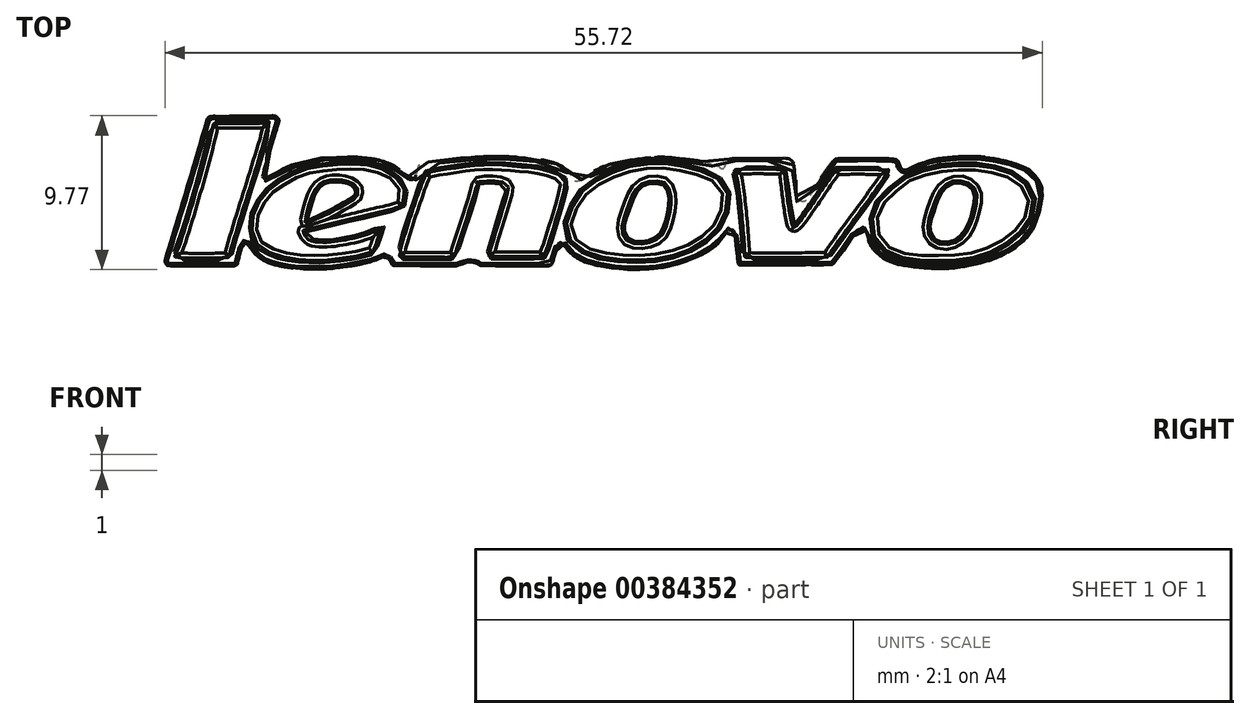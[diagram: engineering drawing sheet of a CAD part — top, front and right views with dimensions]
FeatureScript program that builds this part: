
annotation { "Feature Type Name" : "Feature", "Feature Type Description" : "" }
export const myFeature = defineFeature(function(context is Context, id is Id, definition is map)
    precondition{}
    {
        {
            var Q0;
            Q0=qCreatedBy(makeId("Top.planeOp"),FACE);
            var sketch = newSketch(context, id + "F0", { "sketchPlane" : qUnion([Q0])});
            skFitSpline(sketch, "E0", {"points": [v(-23.1, 6.55) * mm, v(-23.35, 5.6) * mm, v(-23.4, 5.47) * mm, v(-23.53, 5.4) * mm, v(-23.82, 5.4) * mm, v(-27.77, 5.41) * mm, v(-27.88, 5.47) * mm, v(-27.96, 5.64) * mm, v(-27.93, 5.83) * mm, v(-25.31, 14.6) * mm, v(-25.25, 14.76) * mm, v(-25.1, 14.86) * mm, v(-24.75, 14.9) * mm, v(-21.3, 14.92) * mm, v(-20.98, 14.9) * mm, v(-20.82, 14.8) * mm, v(-20.74, 14.67) * mm, v(-20.77, 14.44) * mm, v(-21.75, 11.14) * mm, v(-21.74, 10.99) * mm, v(-21.66, 10.94) * mm, v(-21.44, 10.94) * mm, v(-20.73, 11.4) * mm, v(-19.83, 11.81) * mm, v(-19.1, 12.04) * mm, v(-18.16, 12.23) * mm, v(-17.27, 12.3) * mm, v(-16.19, 12.3) * mm, v(-15.44, 12.26) * mm, v(-14.56, 12.15) * mm, v(-13.8, 11.92) * mm, v(-13.19, 11.6) * mm, v(-12.82, 11.28) * mm, v(-12.63, 11.03) * mm, v(-12.42, 10.87) * mm, v(-12.17, 10.91) * mm, v(-12.08, 11.06) * mm, v(-11.93, 11.4) * mm, v(-11.82, 11.79) * mm, v(-11.59, 11.9) * mm, v(-10.16, 12.15) * mm, v(-8.7, 12.26) * mm, v(-7.2, 12.34) * mm, v(-5.86, 12.3) * mm, v(-4.6, 12.19) * mm, v(-3.59, 12.03) * mm, v(-2.83, 11.74) * mm, v(-2.27, 11.31) * mm, v(-2.1, 10.99) * mm, v(-1.96, 10.8) * mm, v(-1.78, 10.78) * mm, v(-1.62, 10.82) * mm, v(-1.3, 10.99) * mm, v(-0.5, 11.52) * mm, v(0.8, 11.97) * mm, v(2.15, 12.17) * mm, v(3.5, 12.3) * mm, v(4.82, 12.19) * mm, v(6.3, 12) * mm, v(7.15, 11.73) * mm, v(7.45, 11.57) * mm, v(7.63, 11.76) * mm, v(7.8, 12.09) * mm, v(7.93, 12.17) * mm, v(8.77, 12.22) * mm, v(10.88, 12.2) * mm, v(11.6, 12.2) * mm, v(11.86, 12.06) * mm, v(12, 11.74) * mm, v(12.06, 11.2) * mm, v(12.11, 10.45) * mm, v(12.18, 9.67) * mm, v(12.45, 9.5) * mm, v(12.76, 9.58) * mm, v(13.74, 11.05) * mm, v(14.3, 11.83) * mm, v(14.57, 12.15) * mm, v(14.75, 12.19) * mm, v(18.37, 12.16) * mm, v(18.52, 12.09) * mm, v(18.62, 11.98) * mm, v(18.7, 11.73) * mm, v(18.9, 11.5) * mm, v(19.19, 11.5) * mm, v(19.75, 11.77) * mm, v(20.26, 11.95) * mm], "startDerivative": vector(-22.6, -79.97) * mm, "endDerivative": vector(46.12, 13.89) * mm});
            skFitSpline(sketch, "E1", {"points": [v(20.26, 11.95) * mm, v(20.8, 12.12) * mm, v(21.55, 12.24) * mm, v(22.57, 12.33) * mm], "startDerivative": vector(1.82, 0.65) * mm, "endDerivative": vector(2.75, 0.2) * mm});
            skFitSpline(sketch, "E2", {"points": [v(22.57, 12.33) * mm, v(23.76, 12.33) * mm, v(25.15, 12.11) * mm, v(26.09, 11.85) * mm, v(26.85, 11.51) * mm, v(27.47, 10.9) * mm, v(27.74, 10.24) * mm, v(27.6, 8.92) * mm, v(27.13, 7.7) * mm, v(26.29, 6.76) * mm, v(24.84, 5.91) * mm, v(23.43, 5.48) * mm, v(21.77, 5.23) * mm, v(20.26, 5.27) * mm, v(18.82, 5.44) * mm, v(17.78, 5.8) * mm, v(16.93, 6.57) * mm, v(16.67, 7.18) * mm, v(16.59, 7.56) * mm, v(16.5, 7.68) * mm, v(16.1, 7.7) * mm, v(15.95, 7.62) * mm, v(15.49, 6.9) * mm, v(14.9, 6.07) * mm, v(14.45, 5.5) * mm, v(14.3, 5.47) * mm, v(8.6, 5.46) * mm, v(8.44, 5.56) * mm, v(8.19, 7.5) * mm, v(8.08, 7.67) * mm, v(7.95, 7.68) * mm, v(7.77, 7.6) * mm, v(7.35, 7.02) * mm, v(6.44, 6.28) * mm, v(5.38, 5.8) * mm, v(3.76, 5.31) * mm, v(2.27, 5.17) * mm, v(1.03, 5.2) * mm, v(-0.32, 5.38) * mm, v(-1.48, 5.73) * mm, v(-2.23, 6.23) * mm, v(-2.57, 6.64) * mm, v(-2.76, 6.84) * mm, v(-2.92, 6.84) * mm, v(-3.02, 6.69) * mm, v(-3.35, 5.64) * mm, v(-3.45, 5.46) * mm, v(-3.6, 5.38) * mm, v(-3.92, 5.37) * mm, v(-7.82, 5.4) * mm, v(-7.93, 5.42) * mm, v(-8.27, 5.58) * mm, v(-8.78, 5.6) * mm, v(-9.34, 5.43) * mm, v(-9.5, 5.4) * mm, v(-13.36, 5.4) * mm, v(-13.49, 5.42) * mm, v(-13.57, 5.56) * mm, v(-13.8, 5.9) * mm, v(-13.95, 6) * mm, v(-14.04, 6) * mm, v(-14.4, 5.82) * mm, v(-15.04, 5.62) * mm, v(-16.03, 5.4) * mm, v(-17.17, 5.25) * mm, v(-18.19, 5.19) * mm, v(-19.33, 5.22) * mm, v(-20.28, 5.31) * mm, v(-21.1, 5.49) * mm, v(-21.75, 5.77) * mm, v(-22.3, 6.22) * mm, v(-22.56, 6.6) * mm, v(-22.67, 6.77) * mm, v(-22.77, 6.86) * mm, v(-22.92, 6.87) * mm, v(-23.03, 6.77) * mm, v(-23.1, 6.55) * mm], "startDerivative": vector(67.8, 2.63) * mm, "endDerivative": vector(-13.05, -26.65) * mm});
            skFitSpline(sketch, "E3", {"points": [v(20.71, 8.87) * mm, v(21.1, 9.89) * mm, v(21.72, 10.61) * mm, v(22.7, 10.78) * mm, v(23.45, 10.3) * mm, v(23.6, 9.64) * mm, v(23.25, 8.17) * mm, v(22.56, 7.09) * mm, v(21.8, 6.76) * mm, v(20.96, 6.9) * mm, v(20.49, 7.59) * mm, v(20.54, 8.27) * mm, v(20.71, 8.87) * mm]});
            skFitSpline(sketch, "E4", {"points": [v(22.41, 11.78) * mm, v(23.2, 11.8) * mm, v(24.03, 11.71) * mm, v(25.1, 11.49) * mm, v(25.7, 11.28) * mm, v(26.38, 10.9) * mm, v(26.91, 10.3) * mm, v(27.17, 9.58) * mm, v(27, 8.51) * mm, v(26.43, 7.64) * mm, v(25.2, 6.65) * mm, v(23.16, 5.87) * mm, v(21.55, 5.74) * mm, v(19.9, 5.76) * mm, v(18.64, 5.97) * mm, v(17.93, 6.3) * mm, v(17.45, 6.71) * mm, v(17.1, 7.22) * mm, v(16.98, 7.78) * mm, v(17, 8.64) * mm, v(17.36, 9.43) * mm, v(18.06, 10.18) * mm, v(18.82, 10.8) * mm, v(19.7, 11.3) * mm, v(20.44, 11.49) * mm, v(21.36, 11.7) * mm, v(22.41, 11.78) * mm]});
            skFitSpline(sketch, "E5", {"points": [v(8.24, 11.49) * mm, v(11.31, 11.49) * mm, v(11.38, 11.39) * mm, v(11.86, 7.97) * mm, v(11.94, 7.88) * mm, v(12.08, 7.9) * mm, v(14.69, 11.49) * mm, v(14.76, 11.49) * mm, v(15.07, 11.5) * mm, v(17.71, 11.48) * mm, v(17.93, 11.49) * mm, v(18, 11.49) * mm, v(14.18, 6.05) * mm, v(14.03, 5.94) * mm, v(8.92, 5.94) * mm, v(8.85, 6.03) * mm, v(8.27, 11.3) * mm, v(8.24, 11.49) * mm]});
            skFitSpline(sketch, "E6", {"points": [v(7.63, 8.85) * mm, v(7.23, 7.9) * mm, v(6.47, 7.14) * mm, v(5.46, 6.47) * mm, v(4.06, 6) * mm, v(3, 5.8) * mm, v(1.55, 5.75) * mm, v(0.43, 5.86) * mm, v(-0.7, 6.05) * mm, v(-1.74, 6.58) * mm, v(-2.45, 7.4) * mm, v(-2.4, 8.35) * mm, v(-1.91, 9.5) * mm, v(-1.17, 10.4) * mm, v(0, 11.1) * mm, v(1.24, 11.61) * mm, v(2.5, 11.85) * mm, v(3.54, 11.9) * mm, v(4.72, 11.76) * mm, v(5.96, 11.47) * mm, v(6.97, 11.04) * mm, v(7.58, 10.45) * mm, v(7.8, 9.75) * mm, v(7.63, 8.85) * mm]});
            skFitSpline(sketch, "E7", {"points": [v(3.27, 10.78) * mm, v(3.82, 10.64) * mm, v(4.08, 10.23) * mm, v(4.19, 9.59) * mm, v(4.08, 8.68) * mm, v(3.86, 7.87) * mm, v(3.6, 7.36) * mm, v(2.9, 6.9) * mm, v(2.12, 6.79) * mm, v(1.5, 6.91) * mm, v(1.15, 7.32) * mm, v(1.07, 7.98) * mm, v(1.42, 9.13) * mm, v(1.85, 10.14) * mm, v(2.4, 10.64) * mm, v(2.79, 10.77) * mm, v(3.27, 10.78) * mm]});
            skFitSpline(sketch, "E8", {"points": [v(-13.06, 6.08) * mm, v(-11.42, 11.16) * mm, v(-11.28, 11.32) * mm, v(-11, 11.37) * mm, v(-9.84, 11.57) * mm, v(-8.36, 11.76) * mm, v(-7.22, 11.82) * mm, v(-6.24, 11.76) * mm, v(-4.91, 11.64) * mm, v(-4, 11.5) * mm, v(-3.32, 11.3) * mm, v(-2.74, 11.07) * mm, v(-2.57, 10.72) * mm, v(-2.55, 10.47) * mm, v(-2.6, 10.18) * mm, v(-3.86, 6.16) * mm, v(-4, 5.97) * mm, v(-4.14, 5.97) * mm, v(-7.32, 5.99) * mm, v(-7.38, 6.04) * mm, v(-6.18, 10.08) * mm, v(-6.15, 10.35) * mm, v(-6.42, 10.68) * mm, v(-8.13, 10.72) * mm, v(-8.19, 10.55) * mm, v(-9.53, 6.18) * mm, v(-9.6, 5.99) * mm, v(-9.9, 5.95) * mm, v(-12.88, 5.95) * mm, v(-13.06, 6.08) * mm]});
            skFitSpline(sketch, "E9", {"points": [v(-27.26, 6.2) * mm, v(-24.92, 14.24) * mm, v(-24.8, 14.43) * mm, v(-21.66, 14.46) * mm, v(-21.44, 14.37) * mm, v(-23.85, 6.15) * mm, v(-24, 5.93) * mm, v(-27.3, 5.95) * mm, v(-27.26, 6.2) * mm]});
            skFitSpline(sketch, "E10", {"points": [v(-18.98, 8.14) * mm, v(-15.83, 9.75) * mm, v(-15.74, 9.91) * mm, v(-15.7, 10.19) * mm, v(-15.89, 10.5) * mm, v(-16.33, 10.76) * mm, v(-17.01, 10.87) * mm, v(-17.79, 10.78) * mm, v(-18.32, 10.4) * mm, v(-18.7, 9.64) * mm, v(-19.06, 8.33) * mm, v(-18.98, 8.14) * mm]});
            skFitSpline(sketch, "E11", {"points": [v(-19.13, 7.66) * mm, v(-13.01, 9.16) * mm, v(-12.89, 9.27) * mm, v(-12.74, 10.02) * mm, v(-13.03, 10.74) * mm, v(-13.8, 11.39) * mm, v(-15.02, 11.77) * mm, v(-15.9, 11.85) * mm, v(-16.94, 11.83) * mm, v(-18.47, 11.64) * mm, v(-19.43, 11.4) * mm, v(-20.4, 10.9) * mm, v(-21.2, 10.4) * mm, v(-21.7, 9.88) * mm, v(-22.23, 9.05) * mm, v(-22.41, 8.27) * mm, v(-22.41, 7.31) * mm, v(-22.08, 6.72) * mm, v(-21.09, 6.13) * mm, v(-19.63, 5.8) * mm, v(-17.86, 5.75) * mm, v(-16.5, 5.91) * mm, v(-15.26, 6.12) * mm, v(-14.84, 6.28) * mm, v(-14.7, 6.45) * mm, v(-14.25, 7.63) * mm, v(-14.18, 7.8) * mm, v(-14.34, 7.74) * mm, v(-15.35, 7.31) * mm, v(-16.48, 7.06) * mm, v(-17.36, 6.9) * mm, v(-18.3, 6.9) * mm, v(-18.93, 7.13) * mm, v(-19.2, 7.6) * mm, v(-19.13, 7.66) * mm]});
            skLineSegment(sketch, "E12.bottom", {"start": v(-28.07, 12.3) * mm, "end": v(27.8, 12.3) * mm, "construction": true});
            skLineSegment(sketch, "E12.top", {"start": v(-28.07, 5.24) * mm, "end": v(27.8, 5.24) * mm, "construction": true});
            skLineSegment(sketch, "E12.left", {"start": v(-28.07, 12.3) * mm, "end": v(-28.07, 5.24) * mm, "construction": true});
            skLineSegment(sketch, "E12.right", {"start": v(27.8, 12.3) * mm, "end": v(27.8, 5.24) * mm, "construction": true});
            skSolve(sketch);
        }
        {
            var Q0;
            Q0=makeQuery(id+"F0.imprint","IMPRINT",FACE,{"disambiguationData":[TD([[makeQuery(id+"F0.imprint","IMPRINT",EDGE,{"derivedFrom":sQuery(id+"F0.wireOp",EDGE,"E0")}),-1.0]])]});
            var Q1;
            Q1=makeQuery(id+"F0.imprint","IMPRINT",FACE,{"disambiguationData":[TD([[makeQuery(id+"F0.imprint","IMPRINT",EDGE,{"derivedFrom":sQuery(id+"F0.wireOp",EDGE,"E9")}),-1.0]])]});
            var Q2;
            Q2=makeQuery(id+"F0.imprint","IMPRINT",FACE,{"disambiguationData":[TD([[makeQuery(id+"F0.imprint","IMPRINT",EDGE,{"derivedFrom":sQuery(id+"F0.wireOp",EDGE,"E10")}),-1.0]])]});
            var Q3;
            Q3=makeQuery(id+"F0.imprint","IMPRINT",FACE,{"disambiguationData":[TD([[makeQuery(id+"F0.imprint","IMPRINT",EDGE,{"derivedFrom":sQuery(id+"F0.wireOp",EDGE,"E10")}),1.0]])]});
            var Q4;
            Q4=makeQuery(id+"F0.imprint","IMPRINT",FACE,{"disambiguationData":[TD([[makeQuery(id+"F0.imprint","IMPRINT",EDGE,{"derivedFrom":sQuery(id+"F0.wireOp",EDGE,"E8")}),-1.0]])]});
            var Q5;
            Q5=makeQuery(id+"F0.imprint","IMPRINT",FACE,{"disambiguationData":[TD([[makeQuery(id+"F0.imprint","IMPRINT",EDGE,{"derivedFrom":sQuery(id+"F0.wireOp",EDGE,"E6")}),-1.0]])]});
            var Q6;
            Q6=makeQuery(id+"F0.imprint","IMPRINT",FACE,{"disambiguationData":[TD([[makeQuery(id+"F0.imprint","IMPRINT",EDGE,{"derivedFrom":sQuery(id+"F0.wireOp",EDGE,"E7")}),-1.0]])]});
            var Q7;
            Q7=makeQuery(id+"F0.imprint","IMPRINT",FACE,{"disambiguationData":[TD([[makeQuery(id+"F0.imprint","IMPRINT",EDGE,{"derivedFrom":sQuery(id+"F0.wireOp",EDGE,"E5")}),-1.0]])]});
            var Q8;
            Q8=makeQuery(id+"F0.imprint","IMPRINT",FACE,{"disambiguationData":[TD([[makeQuery(id+"F0.imprint","IMPRINT",EDGE,{"derivedFrom":sQuery(id+"F0.wireOp",EDGE,"E3")}),1.0]])]});
            var Q9;
            Q9=makeQuery(id+"F0.imprint","IMPRINT",FACE,{"disambiguationData":[TD([[makeQuery(id+"F0.imprint","IMPRINT",EDGE,{"derivedFrom":sQuery(id+"F0.wireOp",EDGE,"E3")}),-1.0]])]});
            extrude(context, id + "F1", {"entities" : qUnion([Q0, Q1, Q2, Q3, Q4, Q5, Q6, Q7, Q8, Q9]), "depth" : 0.2 * mm});
        }
        {
            var Q0;
            Q0=makeQuery(id+"F0.imprint","IMPRINT",FACE,{"disambiguationData":[TD([[makeQuery(id+"F0.imprint","IMPRINT",EDGE,{"derivedFrom":sQuery(id+"F0.wireOp",EDGE,"E9")}),-1.0]])]});
            var Q1;
            Q1=makeQuery(id+"F0.imprint","IMPRINT",FACE,{"disambiguationData":[TD([[makeQuery(id+"F0.imprint","IMPRINT",EDGE,{"derivedFrom":sQuery(id+"F0.wireOp",EDGE,"E10")}),-1.0]])]});
            var Q2;
            Q2=makeQuery(id+"F0.imprint","IMPRINT",FACE,{"disambiguationData":[TD([[makeQuery(id+"F0.imprint","IMPRINT",EDGE,{"derivedFrom":sQuery(id+"F0.wireOp",EDGE,"E8")}),-1.0]])]});
            var Q3;
            Q3=makeQuery(id+"F0.imprint","IMPRINT",FACE,{"disambiguationData":[TD([[makeQuery(id+"F0.imprint","IMPRINT",EDGE,{"derivedFrom":sQuery(id+"F0.wireOp",EDGE,"E6")}),-1.0]])]});
            var Q4;
            Q4=makeQuery(id+"F0.imprint","IMPRINT",FACE,{"disambiguationData":[TD([[makeQuery(id+"F0.imprint","IMPRINT",EDGE,{"derivedFrom":sQuery(id+"F0.wireOp",EDGE,"E5")}),-1.0]])]});
            var Q5;
            Q5=makeQuery(id+"F0.imprint","IMPRINT",FACE,{"disambiguationData":[TD([[makeQuery(id+"F0.imprint","IMPRINT",EDGE,{"derivedFrom":sQuery(id+"F0.wireOp",EDGE,"E3")}),1.0]])]});
            extrude(context, id + "F2", {"entities" : qUnion([Q0, Q1, Q2, Q3, Q4, Q5]), "operationType" : NewBodyOperationType.ADD, "depth" : 1 * mm});
        }
        {
            var Q0;
            Q0=makeQuery(id+"F2.opExtrude","CAP_EDGE",EDGE,{"disambiguationData":[OSD([sQuery(id+"F0.wireOp",EDGE,"E9")])],"isStart":false});
            var Q1;
            Q1=makeQuery(id+"F2.opExtrude","CAP_EDGE",EDGE,{"disambiguationData":[OSD([sQuery(id+"F0.wireOp",EDGE,"E11")])],"isStart":false});
            var Q2;
            Q2=makeQuery(id+"F2.opExtrude","CAP_EDGE",EDGE,{"disambiguationData":[OSD([sQuery(id+"F0.wireOp",EDGE,"E10")])],"isStart":false});
            var Q3;
            Q3=makeQuery(id+"F2.opExtrude","CAP_EDGE",EDGE,{"disambiguationData":[OSD([sQuery(id+"F0.wireOp",EDGE,"E8")])],"isStart":false});
            var Q4;
            Q4=makeQuery(id+"F2.opExtrude","CAP_EDGE",EDGE,{"disambiguationData":[OSD([sQuery(id+"F0.wireOp",EDGE,"E6")])],"isStart":false});
            var Q5;
            Q5=makeQuery(id+"F2.opExtrude","CAP_EDGE",EDGE,{"disambiguationData":[OSD([sQuery(id+"F0.wireOp",EDGE,"E7")])],"isStart":false});
            var Q6;
            Q6=makeQuery(id+"F2.opExtrude","CAP_EDGE",EDGE,{"disambiguationData":[OSD([sQuery(id+"F0.wireOp",EDGE,"E5")])],"isStart":false});
            var Q7;
            Q7=makeQuery(id+"F2.opExtrude","CAP_EDGE",EDGE,{"disambiguationData":[OSD([sQuery(id+"F0.wireOp",EDGE,"E3")])],"isStart":false});
            var Q8;
            Q8=makeQuery(id+"F2.opExtrude","CAP_EDGE",EDGE,{"disambiguationData":[OSD([sQuery(id+"F0.wireOp",EDGE,"E4")])],"isStart":false});
            fillet(context, id + "F3", {"entities" : qUnion([Q0, Q1, Q2, Q3, Q4, Q5, Q6, Q7, Q8]), "radius" : .3 * mm, "tangentPropagation" : true, "allowEdgeOverflow" : false});
        }
        {
            var Q0;
            {var subQ0=sQuery(id+"F0.wireOp",EDGE,"E2");var subQ1=sQuery(id+"F0.wireOp",EDGE,"E1");var subQ2=sQuery(id+"F0.wireOp",EDGE,"E0");Q0=makeQuery(id+"F2.boolean.opBoolean","SPLIT",FACE,{"disambiguationData":[TD([makeQuery(id+"F1.opExtrude","SWEPT_FACE",FACE,{"disambiguationData":[OSD([subQ2])]})])],"derivedFrom":makeQuery(id+"F1.opExtrude","CAP_FACE",FACE,{"disambiguationData":[OSD([subQ2,subQ1,subQ0])],"isStart":false})});}
            var Q1;
            Q1=makeQuery(id+"F2.boolean.opBoolean","SPLIT",FACE,{"disambiguationData":[TD([makeQuery(id+"F2.opExtrude","SWEPT_FACE",FACE,{"disambiguationData":[OSD([sQuery(id+"F0.wireOp",EDGE,"E10")])]})])],"derivedFrom":makeQuery(id+"F1.opExtrude","CAP_FACE",FACE,{"disambiguationData":[OSD([sQuery(id+"F0.wireOp",EDGE,"E0"),sQuery(id+"F0.wireOp",EDGE,"E1"),sQuery(id+"F0.wireOp",EDGE,"E2")])],"isStart":false})});
            var Q2;
            Q2=makeQuery(id+"F2.boolean.opBoolean","SPLIT",FACE,{"disambiguationData":[TD([makeQuery(id+"F2.opExtrude","SWEPT_FACE",FACE,{"disambiguationData":[OSD([sQuery(id+"F0.wireOp",EDGE,"E3")])]})])],"derivedFrom":makeQuery(id+"F1.opExtrude","CAP_FACE",FACE,{"disambiguationData":[OSD([sQuery(id+"F0.wireOp",EDGE,"E0"),sQuery(id+"F0.wireOp",EDGE,"E1"),sQuery(id+"F0.wireOp",EDGE,"E2")])],"isStart":false})});
            var Q3;
            Q3=makeQuery(id+"F2.boolean.opBoolean","SPLIT",FACE,{"disambiguationData":[TD([makeQuery(id+"F2.opExtrude","SWEPT_FACE",FACE,{"disambiguationData":[OSD([sQuery(id+"F0.wireOp",EDGE,"E7")])]})])],"derivedFrom":makeQuery(id+"F1.opExtrude","CAP_FACE",FACE,{"disambiguationData":[OSD([sQuery(id+"F0.wireOp",EDGE,"E0"),sQuery(id+"F0.wireOp",EDGE,"E1"),sQuery(id+"F0.wireOp",EDGE,"E2")])],"isStart":false})});
            fillet(context, id + "F4", {"entities" : qUnion([Q0, Q1, Q2, Q3]), "radius" : .15 * mm, "tangentPropagation" : true, "allowEdgeOverflow" : false});
        }
    });
